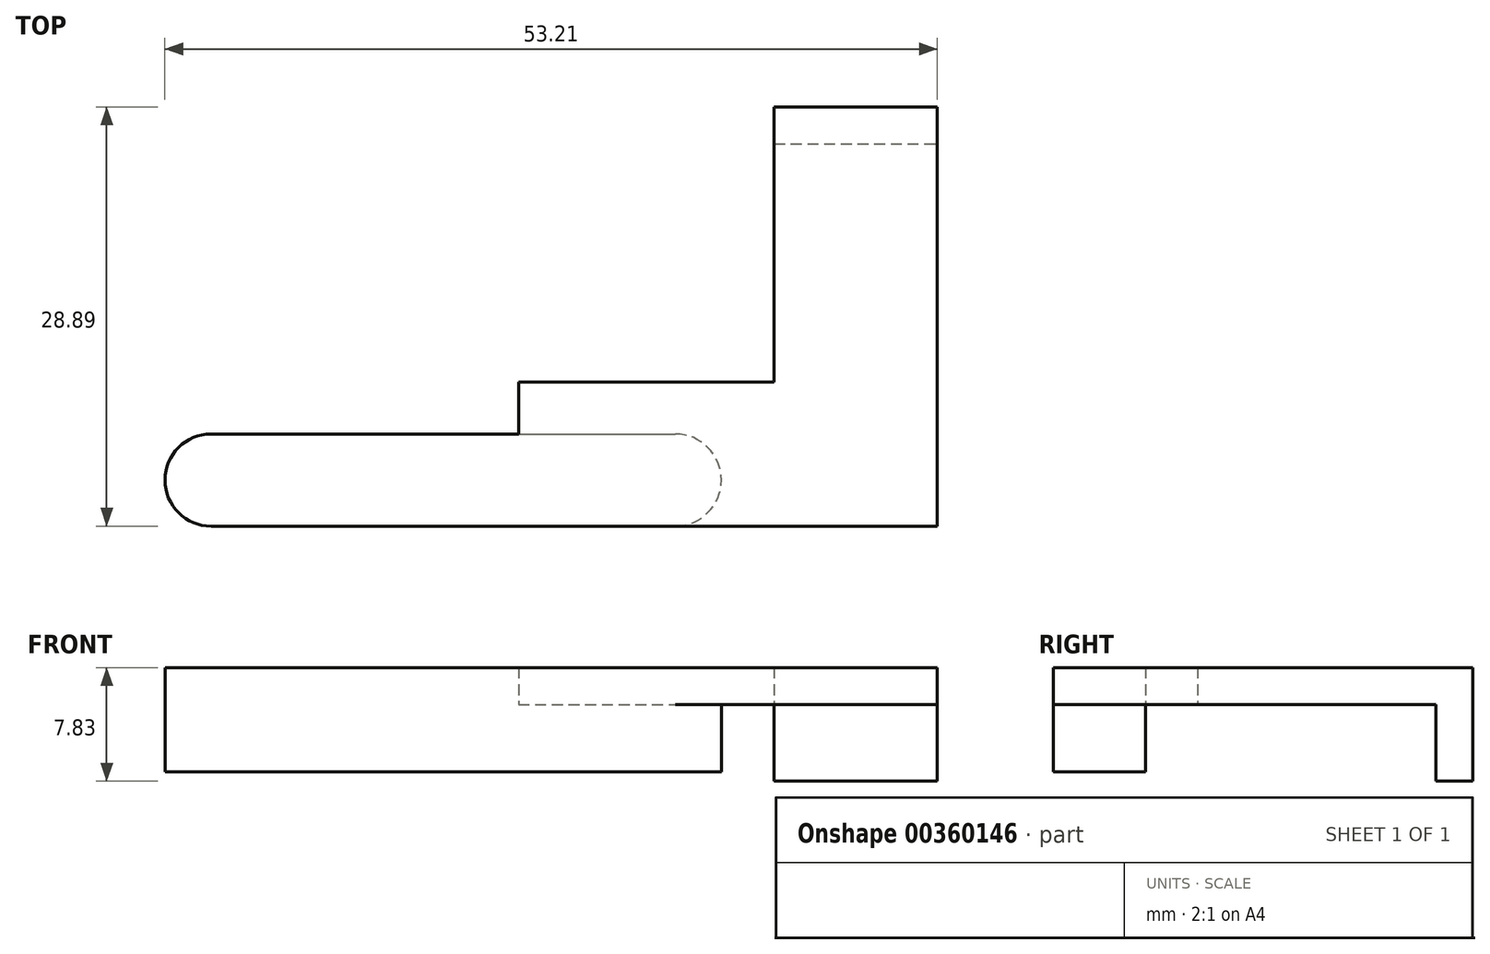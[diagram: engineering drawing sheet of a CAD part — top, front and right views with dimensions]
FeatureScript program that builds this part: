
annotation { "Feature Type Name" : "Feature", "Feature Type Description" : "" }
export const myFeature = defineFeature(function(context is Context, id is Id, definition is map)
    precondition{}
    {
        {
            var Q0;
            Q0=qCreatedBy(makeId("Top.planeOp"),FACE);
            var sketch = newSketch(context, id + "F0", { "sketchPlane" : qUnion([Q0])});
            skLineSegment(sketch, "E0.bottom", {"start": v(0, 0) * mm, "end": v(31.98, 0) * mm});
            skLineSegment(sketch, "E0.top", {"start": v(0, 6.35) * mm, "end": v(31.98, 6.35) * mm});
            skLineSegment(sketch, "E0.left", {"start": v(0, 0) * mm, "end": v(0, 6.35) * mm, "construction": true});
            skLineSegment(sketch, "E0.right", {"start": v(31.98, 0) * mm, "end": v(31.98, 6.35) * mm, "construction": true});
            skArc(sketch, "E1", {"start": v(31.98, 0) * mm, "mid": v(35.15, 3.18) * mm, "end": v(31.98, 6.35) * mm});
            skArc(sketch, "E2", {"start": v(0, 6.35) * mm, "mid": v(-3.18, 3.18) * mm, "end": v(0, 0) * mm});
            skSolve(sketch);
        }
        {
            var Q0;
            Q0=makeQuery(id+"F0.imprint","IMPRINT",FACE,{"disambiguationData":[TD([[makeQuery(id+"F0.imprint","IMPRINT",EDGE,{"derivedFrom":sQuery(id+"F0.wireOp",EDGE,"E0.bottom")}),1.0]])]});
            extrude(context, id + "F1", {"entities" : qUnion([Q0]), "depth" : 4.65 * mm});
        }
        {
            var Q0;
            Q0=makeQuery(id+"F1.opExtrude","CAP_FACE",FACE,{"disambiguationData":[OSD([sQuery(id+"F0.wireOp",EDGE,"E0.bottom"),sQuery(id+"F0.wireOp",EDGE,"E0.top"),sQuery(id+"F0.wireOp",EDGE,"E0.left"),sQuery(id+"F0.wireOp",EDGE,"E1")])],"isStart":false});
            var sketch = newSketch(context, id + "F2", { "sketchPlane" : qUnion([Q0])});
            skLineSegment(sketch, "E3.bottom", {"start": v(35.15, 0) * mm, "end": v(38.79, 0) * mm});
            skLineSegment(sketch, "E3.top", {"start": v(35.15, 9.93) * mm, "end": v(38.79, 9.93) * mm});
            skLineSegment(sketch, "E3.left", {"start": v(35.15, 0) * mm, "end": v(35.15, 9.93) * mm, "construction": true});
            skLineSegment(sketch, "E3.right", {"start": v(38.79, 0) * mm, "end": v(38.79, 9.93) * mm});
            skLineSegment(sketch, "E4", {"start": v(35.15, 0) * mm, "end": v(21.18, 0) * mm});
            skLineSegment(sketch, "E5", {"start": v(21.18, 0) * mm, "end": v(21.18, 9.93) * mm});
            skLineSegment(sketch, "E6", {"start": v(21.18, 9.93) * mm, "end": v(35.15, 9.93) * mm});
            skLineSegment(sketch, "E7.bottom", {"start": v(38.79, 0) * mm, "end": v(50.03, 0) * mm});
            skLineSegment(sketch, "E7.top", {"start": v(38.79, 28.9) * mm, "end": v(50.03, 28.9) * mm});
            skLineSegment(sketch, "E7.left", {"start": v(38.79, 0) * mm, "end": v(38.79, 28.9) * mm});
            skLineSegment(sketch, "E7.right", {"start": v(50.03, 0) * mm, "end": v(50.03, 28.9) * mm});
            skLineSegment(sketch, "E8", {"start": v(38.79, 26.35) * mm, "end": v(50.03, 26.35) * mm});
            skSolve(sketch);
        }
        {
            var Q0;
            {var subQ3=sQuery(id+"F2.wireOp",EDGE,"E7.bottom");Q0=makeQuery(id+"F2.imprint","IMPRINT",FACE,{"disambiguationData":[TD([[makeQuery(id+"F2.imprint","IMPRINT",EDGE,{"derivedFrom":subQ3}),1.0]])]});}
            var Q1;
            {var subQ2=sQuery(id+"F2.wireOp",EDGE,"E3.bottom");Q1=makeQuery(id+"F2.imprint","IMPRINT",FACE,{"disambiguationData":[TD([[makeQuery(id+"F2.imprint","IMPRINT",EDGE,{"derivedFrom":subQ2}),1.0]])]});}
            var Q2;
            {var subQ1=makeQuery(id+"F1.opExtrude","CAP_EDGE",EDGE,{"disambiguationData":[OSD([sQuery(id+"F0.wireOp",EDGE,"E1")])],"isStart":false});Q2=makeQuery(id+"F2.imprint","IMPRINT",FACE,{"disambiguationData":[TD([[makeQuery(id+"F2.imprint","IMPRINT",EDGE,{"derivedFrom":subQ1}),1.0]])]});}
            var Q3;
            {var subQ0=sQuery(id+"F2.wireOp",EDGE,"E7.top");Q3=makeQuery(id+"F2.imprint","IMPRINT",FACE,{"disambiguationData":[TD([[makeQuery(id+"F2.imprint","IMPRINT",EDGE,{"derivedFrom":subQ0}),-1.0]])]});}
            var Q4;
            {var subQ5=makeQuery(id+"F1.opExtrude","CAP_EDGE",EDGE,{"disambiguationData":[OSD([sQuery(id+"F0.wireOp",EDGE,"E0.left")])],"isStart":false});Q4=makeQuery(id+"F2.imprint","IMPRINT",FACE,{"disambiguationData":[TD([[makeQuery(id+"F2.imprint","IMPRINT",EDGE,{"derivedFrom":subQ5}),-1.0]])]});}
            var Q5;
            {var subQ5=makeQuery(id+"F1.opExtrude","CAP_EDGE",EDGE,{"disambiguationData":[OSD([sQuery(id+"F0.wireOp",EDGE,"E2")])],"isStart":false});Q5=makeQuery(id+"F2.imprint","IMPRINT",FACE,{"disambiguationData":[TD([[makeQuery(id+"F2.imprint","IMPRINT",EDGE,{"derivedFrom":subQ5}),1.0]])]});}
            extrude(context, id + "F3", {"entities" : qUnion([Q0, Q1, Q2, Q3, Q4, Q5]), "operationType" : NewBodyOperationType.ADD, "depth" : 2.54 * mm});
        }
        {
            var Q0;
            {var subQ0=sQuery(id+"F2.wireOp",EDGE,"E7.top");Q0=makeQuery(id+"F2.imprint","IMPRINT",FACE,{"disambiguationData":[TD([[makeQuery(id+"F2.imprint","IMPRINT",EDGE,{"derivedFrom":subQ0}),-1.0]])]});}
            extrude(context, id + "F4", {"entities" : qUnion([Q0]), "operationType" : NewBodyOperationType.ADD, "oppositeDirection" : true, "depth" : 5.28 * mm});
        }
    });
